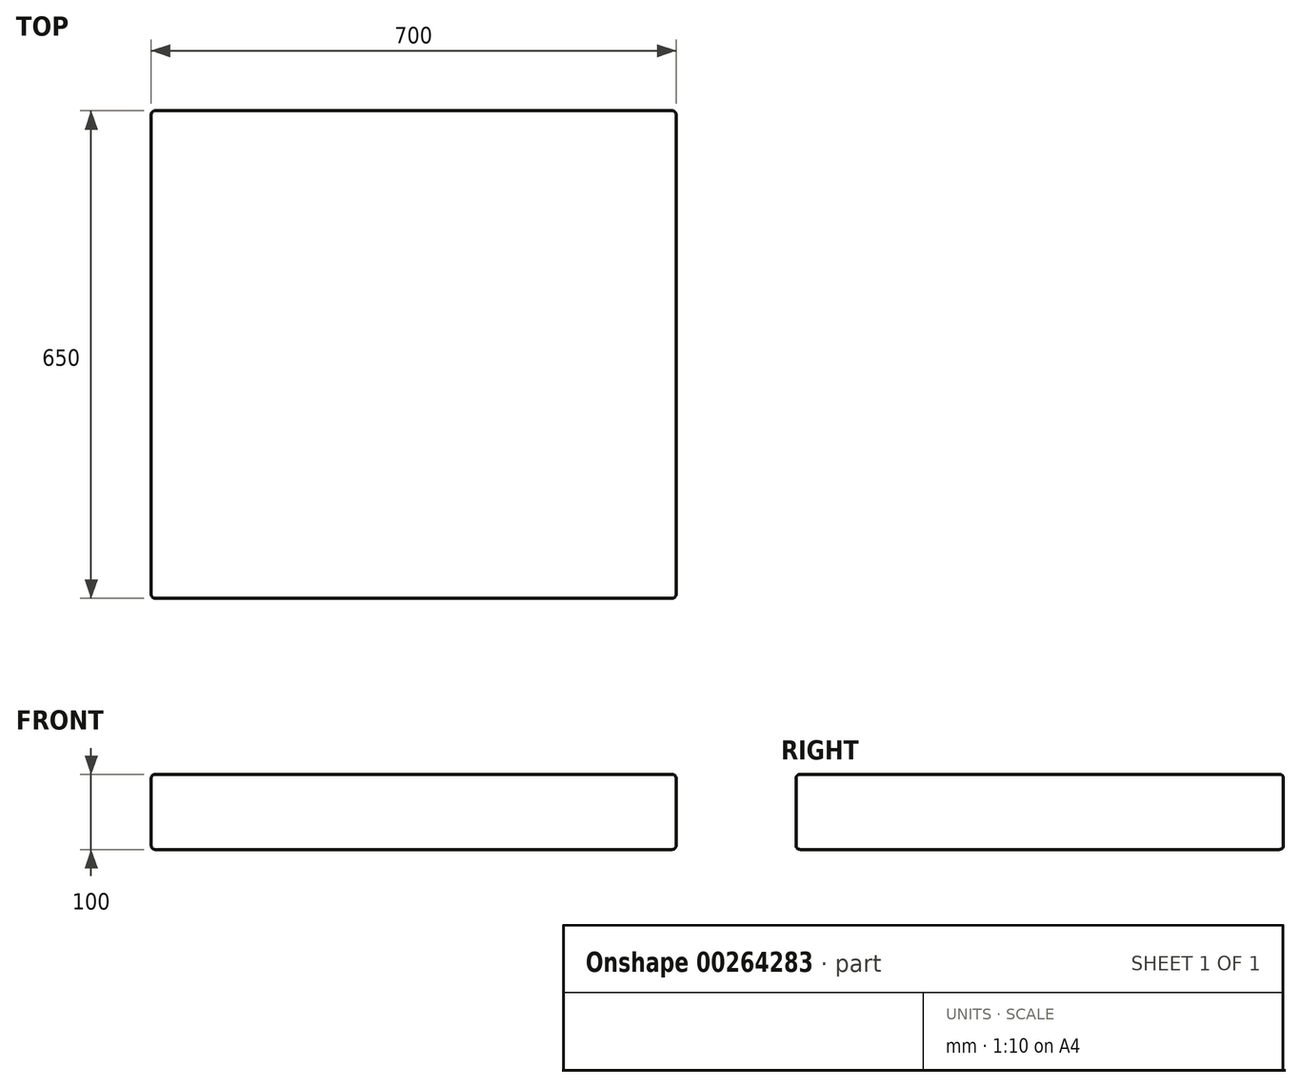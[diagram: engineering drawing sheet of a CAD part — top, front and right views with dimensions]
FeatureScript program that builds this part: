
annotation { "Feature Type Name" : "Feature", "Feature Type Description" : "" }
export const myFeature = defineFeature(function(context is Context, id is Id, definition is map)
    precondition{}
    {
        {
            var Q0;
            Q0=qCreatedBy(makeId("Top.planeOp"),FACE);
            var sketch = newSketch(context, id + "F0", { "sketchPlane" : qUnion([Q0])});
            skLineSegment(sketch, "E0.bottom", {"start": v(-350, 325) * mm, "end": v(350, 325) * mm});
            skLineSegment(sketch, "E0.top", {"start": v(-350, -325) * mm, "end": v(350, -325) * mm});
            skLineSegment(sketch, "E0.left", {"start": v(-350, 325) * mm, "end": v(-350, -325) * mm});
            skLineSegment(sketch, "E0.right", {"start": v(350, 325) * mm, "end": v(350, -325) * mm});
            skLineSegment(sketch, "E1", {"start": v(0, 325) * mm, "end": v(0, -325) * mm, "construction": true});
            skLineSegment(sketch, "E2", {"start": v(-350, 0) * mm, "end": v(350, 0) * mm, "construction": true});
            skSolve(sketch);
        }
        {
            var Q0;
            Q0=makeQuery(id+"F0.imprint","IMPRINT",FACE,{"disambiguationData":[TD([[makeQuery(id+"F0.imprint","IMPRINT",EDGE,{"derivedFrom":sQuery(id+"F0.wireOp",EDGE,"E0.bottom")}),-1.0]])]});
            extrude(context, id + "F1", {"entities" : qUnion([Q0]), "endBound" : BoundingType.SYMMETRIC, "depth" : 100 * mm});
        }
        {
            var Q0;
            Q0=makeQuery(id+"F1.opExtrude","CAP_EDGE",EDGE,{"disambiguationData":[OSD([sQuery(id+"F0.wireOp",EDGE,"E0.top")])],"isStart":false});
            var Q1;
            Q1=makeQuery(id+"F1.opExtrude","CAP_EDGE",EDGE,{"disambiguationData":[OSD([sQuery(id+"F0.wireOp",EDGE,"E0.left")])],"isStart":false});
            var Q2;
            Q2=makeQuery(id+"F1.opExtrude","CAP_EDGE",EDGE,{"disambiguationData":[OSD([sQuery(id+"F0.wireOp",EDGE,"E0.bottom")])],"isStart":false});
            var Q3;
            Q3=makeQuery(id+"F1.opExtrude","CAP_EDGE",EDGE,{"disambiguationData":[OSD([sQuery(id+"F0.wireOp",EDGE,"E0.right")])],"isStart":false});
            var Q4;
            Q4=makeQuery(id+"F1.opExtrude","CAP_EDGE",EDGE,{"disambiguationData":[OSD([sQuery(id+"F0.wireOp",EDGE,"E0.right")])],"isStart":true});
            var Q5;
            Q5=makeQuery(id+"F1.opExtrude","CAP_EDGE",EDGE,{"disambiguationData":[OSD([sQuery(id+"F0.wireOp",EDGE,"E0.top")])],"isStart":true});
            var Q6;
            Q6=makeQuery(id+"F1.opExtrude","SWEPT_EDGE",EDGE,{"disambiguationData":[OSD([sQuery(id+"F0.wireOp",EDGE,"E0.top"),sQuery(id+"F0.wireOp",EDGE,"E0.right")])]});
            var Q7;
            Q7=makeQuery(id+"F1.opExtrude","SWEPT_EDGE",EDGE,{"disambiguationData":[OSD([sQuery(id+"F0.wireOp",EDGE,"E0.top"),sQuery(id+"F0.wireOp",EDGE,"E0.left")])]});
            var Q8;
            Q8=makeQuery(id+"F1.opExtrude","SWEPT_EDGE",EDGE,{"disambiguationData":[OSD([sQuery(id+"F0.wireOp",EDGE,"E0.bottom"),sQuery(id+"F0.wireOp",EDGE,"E0.right")])]});
            var Q9;
            Q9=makeQuery(id+"F1.opExtrude","CAP_EDGE",EDGE,{"disambiguationData":[OSD([sQuery(id+"F0.wireOp",EDGE,"E0.bottom")])],"isStart":true});
            var Q10;
            Q10=makeQuery(id+"F1.opExtrude","SWEPT_EDGE",EDGE,{"disambiguationData":[OSD([sQuery(id+"F0.wireOp",EDGE,"E0.bottom"),sQuery(id+"F0.wireOp",EDGE,"E0.left")])]});
            var Q11;
            Q11=makeQuery(id+"F1.opExtrude","CAP_EDGE",EDGE,{"disambiguationData":[OSD([sQuery(id+"F0.wireOp",EDGE,"E0.left")])],"isStart":true});
            fillet(context, id + "F2", {"entities" : qUnion([Q0, Q1, Q2, Q3, Q4, Q5, Q6, Q7, Q8, Q9, Q10, Q11]), "radius" : 5 * mm, "tangentPropagation" : true, "allowEdgeOverflow" : false});
        }
    });
